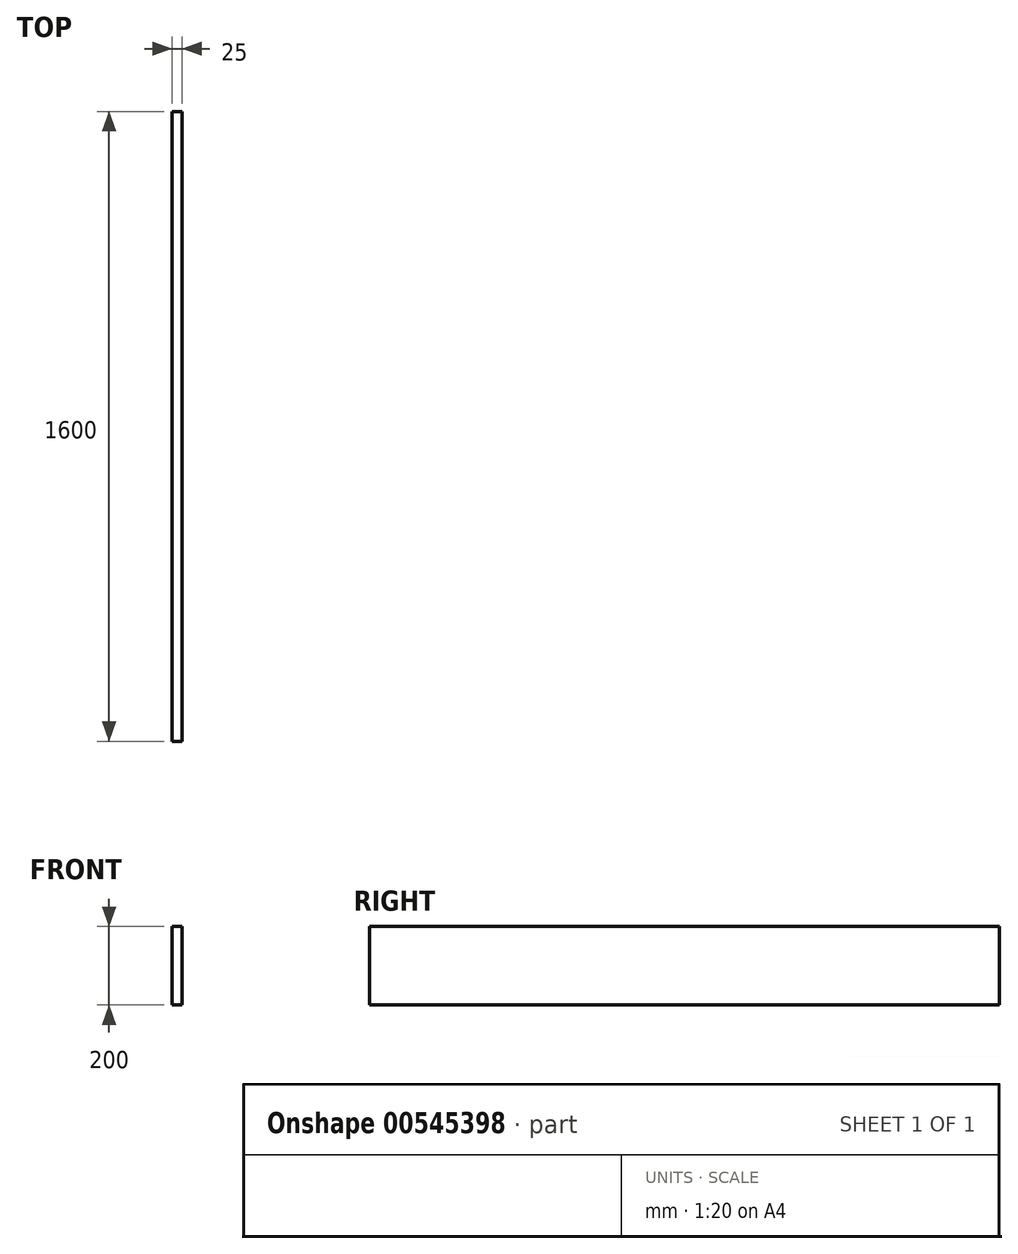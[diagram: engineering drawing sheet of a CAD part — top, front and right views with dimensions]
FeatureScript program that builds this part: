
annotation { "Feature Type Name" : "Feature", "Feature Type Description" : "" }
export const myFeature = defineFeature(function(context is Context, id is Id, definition is map)
    precondition{}
    {
        {
            var Q0;
            Q0=qCreatedBy(makeId("Top.planeOp"),FACE);
            var sketch = newSketch(context, id + "F0", { "sketchPlane" : qUnion([Q0])});
            skLineSegment(sketch, "E0.bottom", {"start": v(0, 0) * mm, "end": v(25, 0) * mm});
            skLineSegment(sketch, "E0.top", {"start": v(0, 1600) * mm, "end": v(25, 1600) * mm});
            skLineSegment(sketch, "E0.left", {"start": v(0, 0) * mm, "end": v(0, 1600) * mm});
            skLineSegment(sketch, "E0.right", {"start": v(25, 0) * mm, "end": v(25, 1600) * mm});
            skSolve(sketch);
        }
        {
            var Q0;
            Q0=qSketchRegion(id+"F0",true);
            extrude(context, id + "F1", {"entities" : qUnion([Q0]), "depth" : 200 * mm, "offsetDistance" : 25 * mm});
        }
    });
